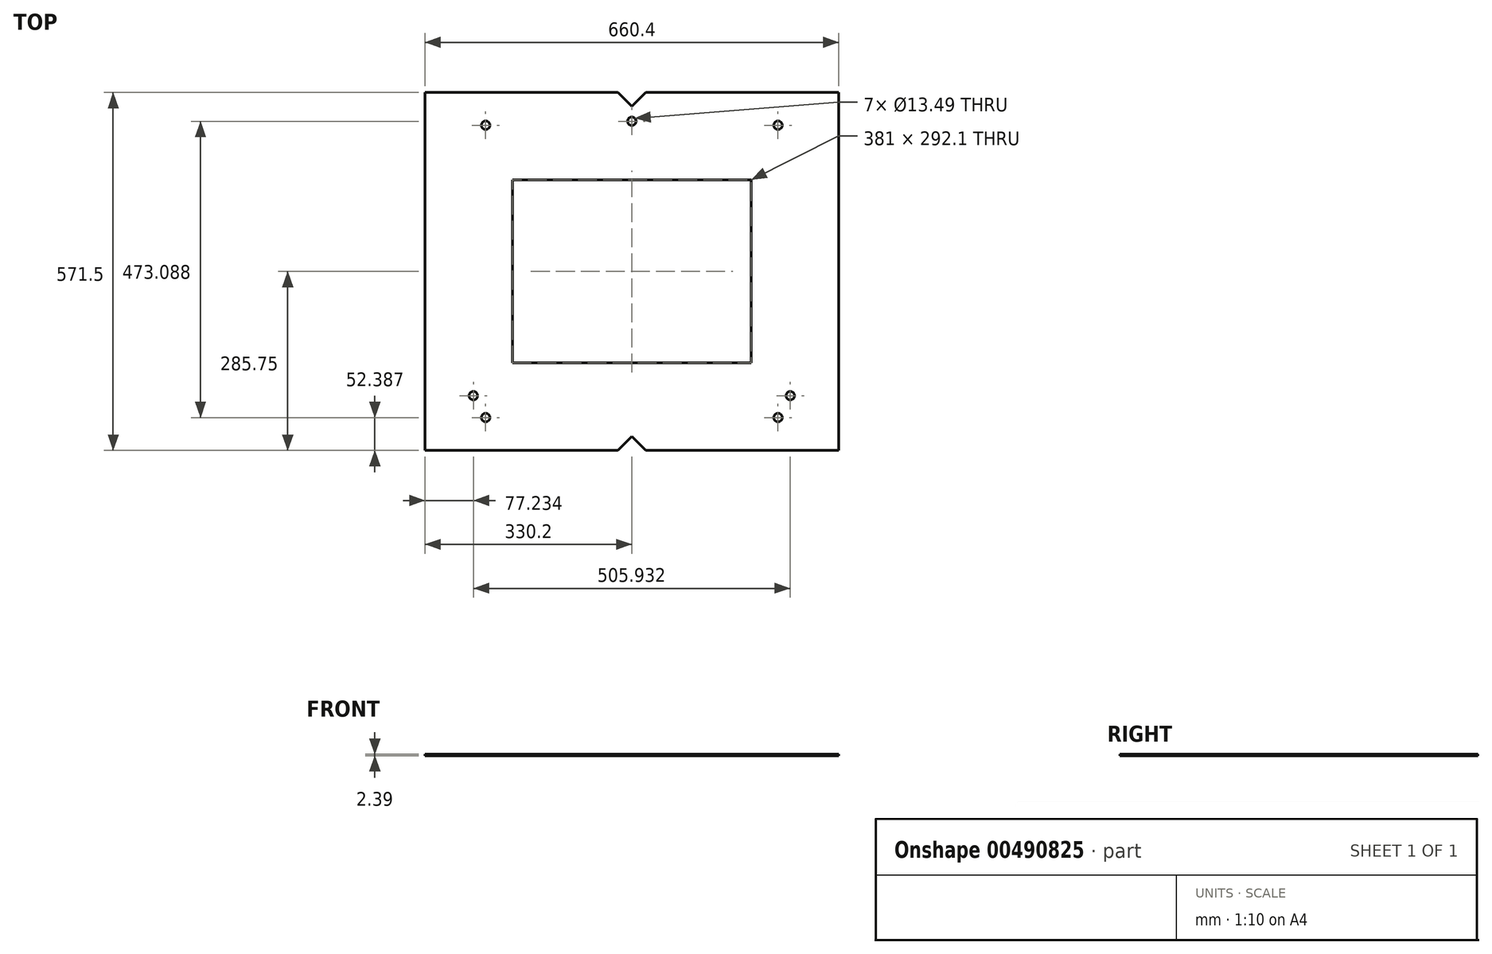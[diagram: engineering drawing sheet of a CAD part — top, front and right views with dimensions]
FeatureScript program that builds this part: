
annotation { "Feature Type Name" : "Feature", "Feature Type Description" : "" }
export const myFeature = defineFeature(function(context is Context, id is Id, definition is map)
    precondition{}
    {
        {
            var Q0;
            Q0=qCreatedBy(makeId("Top.planeOp"),FACE);
            var sketch = newSketch(context, id + "F0", { "sketchPlane" : qUnion([Q0])});
            skLineSegment(sketch, "E0.bottom", {"start": v(-330.2, 285.75) * mm, "end": v(330.2, 285.75) * mm});
            skLineSegment(sketch, "E0.top", {"start": v(-330.2, -285.75) * mm, "end": v(330.2, -285.75) * mm});
            skLineSegment(sketch, "E0.left", {"start": v(-330.2, 285.75) * mm, "end": v(-330.2, -285.75) * mm});
            skLineSegment(sketch, "E0.right", {"start": v(330.2, 285.75) * mm, "end": v(330.2, -285.75) * mm});
            skCircle(sketch, "E1", {"center": v(-233.36, 233.36) * mm, "radius": 6.75 * mm});
            skCircle(sketch, "E2", {"center": v(233.36, 233.36) * mm, "radius": 6.75 * mm});
            skCircle(sketch, "E3", {"center": v(233.36, -233.36) * mm, "radius": 6.75 * mm});
            skCircle(sketch, "E4", {"center": v(-233.36, -233.36) * mm, "radius": 6.75 * mm});
            skCircle(sketch, "E5", {"center": v(-252.97, -198.42) * mm, "radius": 6.75 * mm});
            skCircle(sketch, "E6", {"center": v(252.97, -198.42) * mm, "radius": 6.75 * mm});
            skCircle(sketch, "E7", {"center": v(0, 0) * mm, "radius": 330.02 * mm, "construction": true});
            skCircle(sketch, "E8", {"center": v(0, 239.73) * mm, "radius": 6.75 * mm});
            skCircle(sketch, "E9", {"center": v(0, -52.37) * mm, "radius": 292.1 * mm, "construction": true});
            skLineSegment(sketch, "E10", {"start": v(-330.2, -215.9) * mm, "end": v(330.2, -215.9) * mm, "construction": true});
            skLineSegment(sketch, "E11", {"start": v(-330.2, 215.9) * mm, "end": v(330.2, 215.9) * mm, "construction": true});
            skLineSegment(sketch, "E12", {"start": v(-252.97, -198.42) * mm, "end": v(0, -52.37) * mm, "construction": true});
            skLineSegment(sketch, "E13", {"start": v(0, 239.73) * mm, "end": v(0, -52.37) * mm, "construction": true});
            skSolve(sketch);
        }
        {
            var Q0;
            Q0=makeQuery(id+"F0.imprint","IMPRINT",FACE,{"disambiguationData":[TD([[makeQuery(id+"F0.imprint","IMPRINT",EDGE,{"derivedFrom":sQuery(id+"F0.wireOp",EDGE,"E0.bottom")}),-1.0]])]});
            extrude(context, id + "F1", {"entities" : qUnion([Q0]), "oppositeDirection" : true, "depth" : 2.4 * mm});
        }
        {
            var Q0;
            Q0=qCreatedBy(makeId("Top.planeOp"),FACE);
            var sketch = newSketch(context, id + "F2", { "sketchPlane" : qUnion([Q0])});
            skLineSegment(sketch, "E14", {"start": v(-22.22, 285.75) * mm, "end": v(0, 263.53) * mm});
            skLineSegment(sketch, "E15", {"start": v(0, 263.53) * mm, "end": v(22.23, 285.75) * mm});
            skLineSegment(sketch, "E16", {"start": v(22.23, 285.75) * mm, "end": v(-22.22, 285.75) * mm});
            skLineSegment(sketch, "E17", {"start": v(-330.2, 0) * mm, "end": v(330.2, 0) * mm, "construction": true});
            skLineSegment(sketch, "E18.MirrorCS", {"start": v(22.23, -285.75) * mm, "end": v(-22.22, -285.75) * mm});
            skLineSegment(sketch, "E19.MirrorCS", {"start": v(-22.22, -285.75) * mm, "end": v(0, -263.53) * mm});
            skLineSegment(sketch, "E20.MirrorCS", {"start": v(0, -263.53) * mm, "end": v(22.23, -285.75) * mm});
            skSolve(sketch);
        }
        {
            var Q0;
            Q0 = qSketchRegion(id + "F2", true);
            extrude(context, id + "F3", {"entities" : qUnion([Q0]), "operationType" : NewBodyOperationType.REMOVE, "endBound" : BoundingType.THROUGH_ALL, "oppositeDirection" : true, "depth" : 25.4 * mm});
        }
        {
            var Q0;
            Q0=qCreatedBy(makeId("Top.planeOp"),FACE);
            var sketch = newSketch(context, id + "F4", { "sketchPlane" : qUnion([Q0])});
            skLineSegment(sketch, "E21.bottom", {"start": v(-190.5, 146.05) * mm, "end": v(190.5, 146.05) * mm});
            skLineSegment(sketch, "E21.top", {"start": v(-190.5, -146.05) * mm, "end": v(190.5, -146.05) * mm});
            skLineSegment(sketch, "E21.left", {"start": v(-190.5, 146.05) * mm, "end": v(-190.5, -146.05) * mm});
            skLineSegment(sketch, "E21.right", {"start": v(190.5, 146.05) * mm, "end": v(190.5, -146.05) * mm});
            skSolve(sketch);
        }
        {
            var Q0;
            Q0 = qSketchRegion(id + "F4", true);
            extrude(context, id + "F5", {"entities" : qUnion([Q0]), "operationType" : NewBodyOperationType.REMOVE, "endBound" : BoundingType.THROUGH_ALL, "oppositeDirection" : true, "depth" : 25.4 * mm});
        }
    });
